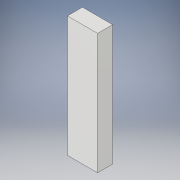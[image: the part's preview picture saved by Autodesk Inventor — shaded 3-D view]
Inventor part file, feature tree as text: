
AUTODESK INVENTOR PART (.ipt)
format: ipt  version: 2017 (Build 210142000, 142)  size: 90,112 bytes
history: native  units: in
note: dims shown in document units (in); Inventor stores cm internally (conversion verified against a paired STEP export)
features: extrude x1, sketch x1
ambient origin geometry x8: Origin, YZ Plane, XZ Plane, XY Plane, X Axis, Y Axis, Z Axis, Center Point
bodies: Solid1 (feature_tree)
feature tree (2):
  extrude  "Extrusion1"  Depth=0.75in
  sketch  "Sketch1"  dims[d0=1.5in d1=0.75in d2=6.0in d3=0.0in]
